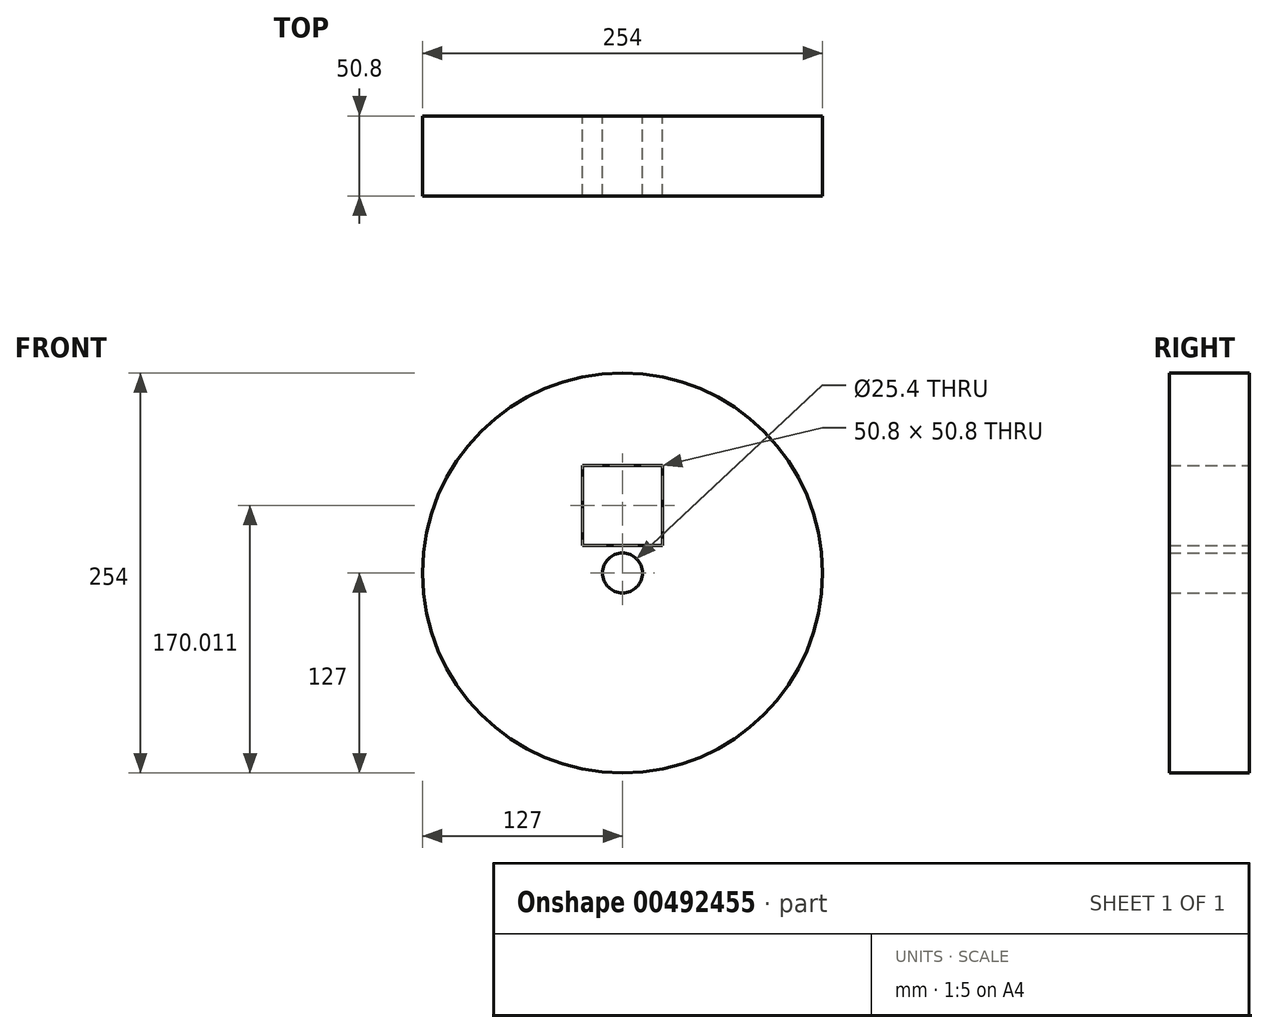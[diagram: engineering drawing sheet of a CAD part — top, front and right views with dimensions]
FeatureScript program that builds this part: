
annotation { "Feature Type Name" : "Feature", "Feature Type Description" : "" }
export const myFeature = defineFeature(function(context is Context, id is Id, definition is map)
    precondition{}
    {
        {
            var Q0;
            Q0=qCreatedBy(makeId("Front.planeOp"),FACE);
            var sketch = newSketch(context, id + "F0", { "sketchPlane" : qUnion([Q0])});
            skCircle(sketch, "E0", {"center": v(0, 0) * mm, "radius": 127 * mm});
            skCircle(sketch, "E1", {"center": v(0, 0) * mm, "radius": 12.7 * mm});
            skSolve(sketch);
        }
        {
            var Q0;
            Q0 = qSketchRegion(id + "F0", true);
            extrude(context, id + "F1", {"entities" : qUnion([Q0]), "endBound" : BoundingType.SYMMETRIC, "depth" : 50.8 * mm});
        }
        {
            var Q0;
            Q0=qCreatedBy(makeId("Front.planeOp"),FACE);
            var sketch = newSketch(context, id + "F2", { "sketchPlane" : qUnion([Q0])});
            skLineSegment(sketch, "E2.bottom", {"start": v(25.4, 68.41) * mm, "end": v(-25.4, 68.41) * mm});
            skLineSegment(sketch, "E2.top", {"start": v(25.4, 17.61) * mm, "end": v(-25.4, 17.61) * mm});
            skLineSegment(sketch, "E2.left", {"start": v(25.4, 68.41) * mm, "end": v(25.4, 17.61) * mm});
            skLineSegment(sketch, "E2.right", {"start": v(-25.4, 68.41) * mm, "end": v(-25.4, 17.61) * mm});
            skPoint(sketch, "E2.middle", {"position": v(0, 43.01) * mm});
            skSolve(sketch);
        }
        {
            var Q0;
            Q0 = qSketchRegion(id + "F2", true);
            extrude(context, id + "F3", {"entities" : qUnion([Q0]), "operationType" : NewBodyOperationType.REMOVE, "endBound" : BoundingType.SYMMETRIC, "depth" : 50.8 * mm});
        }
    });
